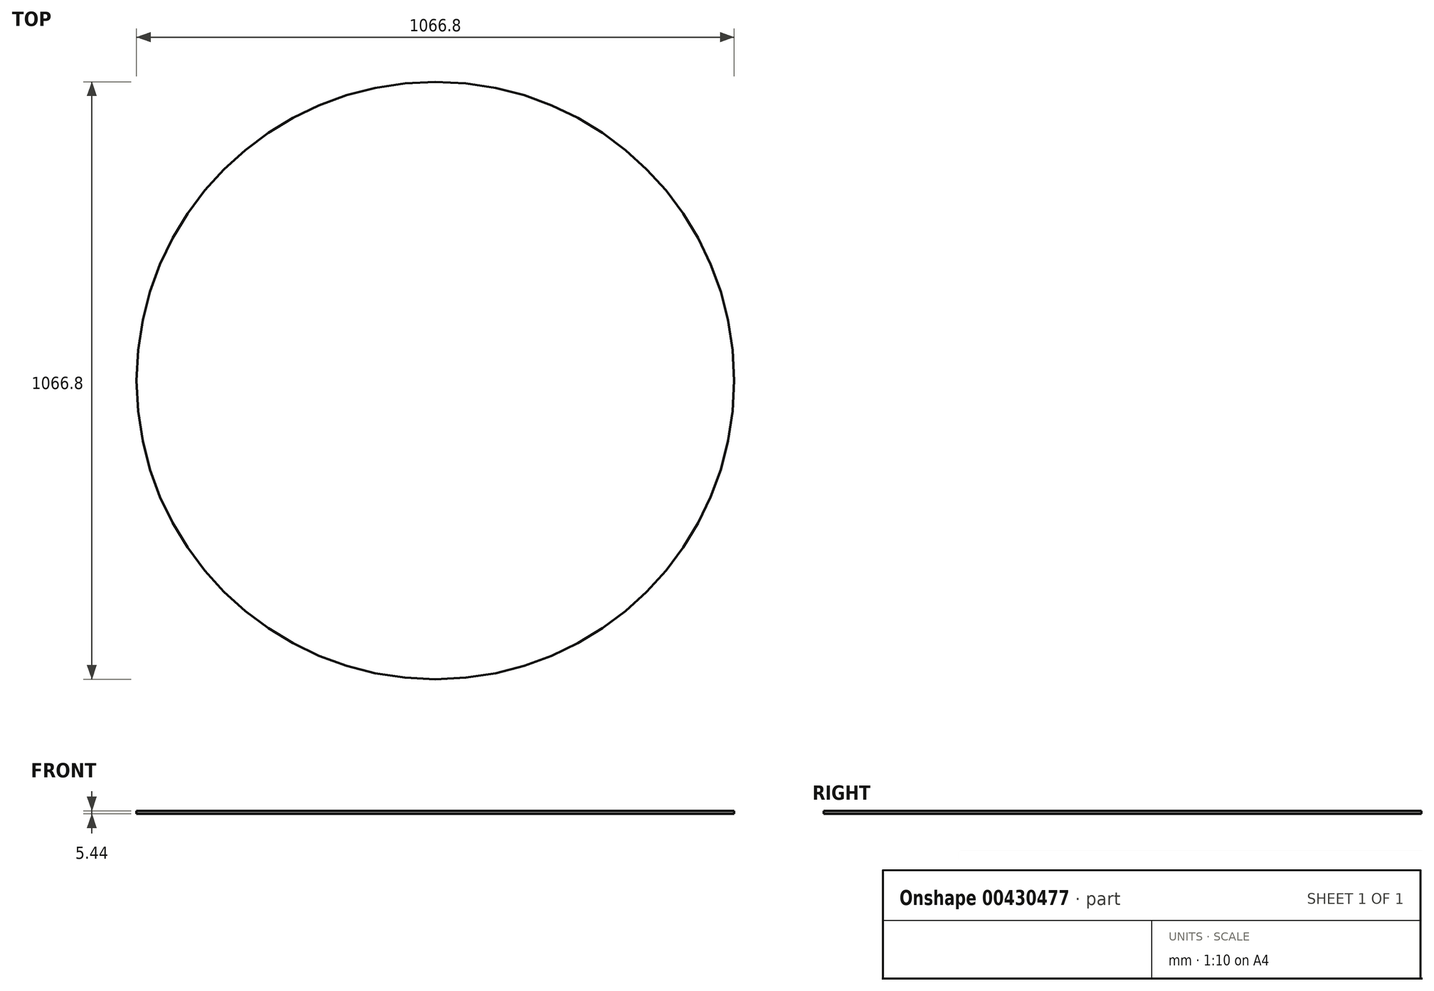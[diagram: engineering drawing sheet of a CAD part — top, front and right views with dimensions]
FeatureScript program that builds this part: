
annotation { "Feature Type Name" : "Feature", "Feature Type Description" : "" }
export const myFeature = defineFeature(function(context is Context, id is Id, definition is map)
    precondition{}
    {
        {
            var Q0;
            Q0=qCreatedBy(makeId("Top.planeOp"),FACE);
            var sketch = newSketch(context, id + "F0", { "sketchPlane" : qUnion([Q0])});
            skCircle(sketch, "E0", {"center": v(0, 0) * mm, "radius": 533.4 * mm});
            skSolve(sketch);
        }
        {
            var Q0;
            Q0=makeQuery(id+"F0.imprint","IMPRINT",FACE,{"disambiguationData":[TD([[makeQuery(id+"F0.imprint","IMPRINT",EDGE,{"derivedFrom":sQuery(id+"F0.wireOp",EDGE,"E0")}),1.0]])]});
            extrude(context, id + "F1", {"entities" : qUnion([Q0]), "depth" : 5.44 * mm});
        }
    });
